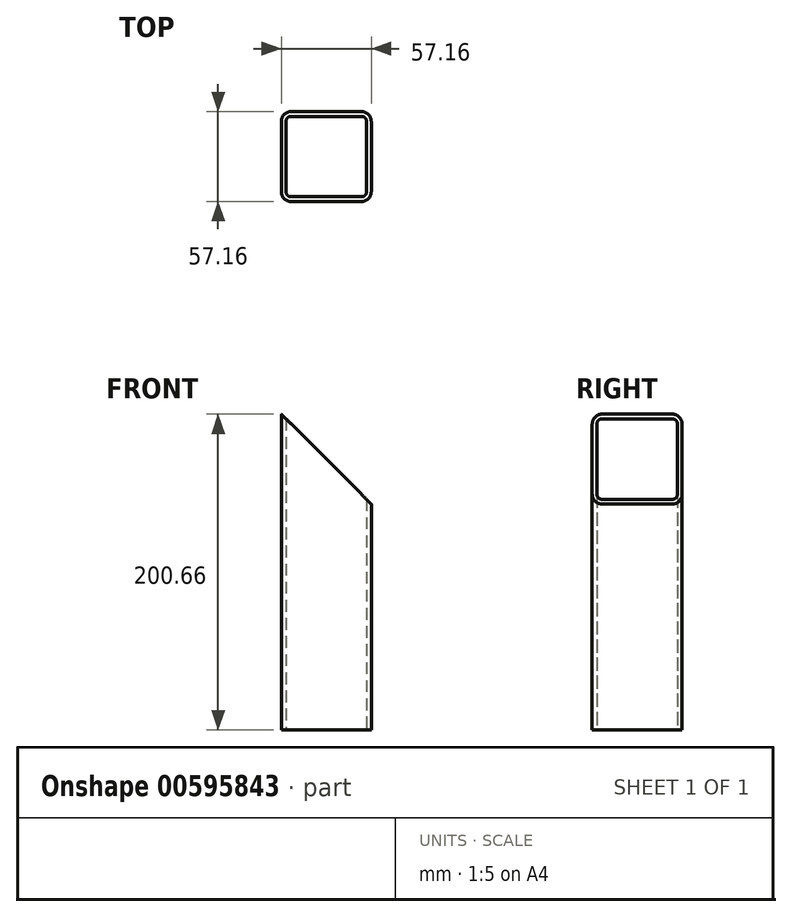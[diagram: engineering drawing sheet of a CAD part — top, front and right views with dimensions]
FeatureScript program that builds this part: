
annotation { "Feature Type Name" : "Feature", "Feature Type Description" : "" }
export const myFeature = defineFeature(function(context is Context, id is Id, definition is map)
    precondition{}
    {
        {
            var Q0;
            Q0=qCreatedBy(makeId("Top.planeOp"),FACE);
            var sketch = newSketch(context, id + "F0", { "sketchPlane" : qUnion([Q0])});
            skLineSegment(sketch, "E0.bottom", {"start": v(28.58, -28.58) * mm, "end": v(-28.58, -28.58) * mm});
            skLineSegment(sketch, "E0.top", {"start": v(28.58, 28.58) * mm, "end": v(-28.58, 28.58) * mm});
            skLineSegment(sketch, "E0.left", {"start": v(28.58, -28.58) * mm, "end": v(28.58, 28.58) * mm});
            skLineSegment(sketch, "E0.right", {"start": v(-28.57, -28.58) * mm, "end": v(-28.58, 28.58) * mm});
            skPoint(sketch, "E0.middle", {"position": v(0, 0) * mm});
            skLineSegment(sketch, "E1.bottom", {"start": v(-25.53, 25.53) * mm, "end": v(25.53, 25.53) * mm});
            skLineSegment(sketch, "E1.top", {"start": v(-25.53, -25.53) * mm, "end": v(25.53, -25.53) * mm});
            skLineSegment(sketch, "E1.left", {"start": v(-25.53, 25.53) * mm, "end": v(-25.53, -25.53) * mm});
            skLineSegment(sketch, "E1.right", {"start": v(25.53, 25.53) * mm, "end": v(25.53, -25.53) * mm});
            skSolve(sketch);
        }
        {
            var Q0;
            Q0=qSketchRegion(id+"F0",true);
            extrude(context, id + "F1", {"entities" : qUnion([Q0]), "depth" : 200.66 * mm, "offsetDistance" : 25.4 * mm});
        }
        {
            var Q0;
            Q0=makeQuery(id+"F1.opExtrude","SWEPT_EDGE",EDGE,{"disambiguationData":[OSD([sQuery(id+"F0.wireOp",EDGE,"E1.bottom"),sQuery(id+"F0.wireOp",EDGE,"E1.right")])]});
            var Q1;
            Q1=makeQuery(id+"F1.opExtrude","SWEPT_EDGE",EDGE,{"disambiguationData":[OSD([sQuery(id+"F0.wireOp",EDGE,"E1.bottom"),sQuery(id+"F0.wireOp",EDGE,"E1.left")])]});
            var Q2;
            Q2=makeQuery(id+"F1.opExtrude","SWEPT_EDGE",EDGE,{"disambiguationData":[OSD([sQuery(id+"F0.wireOp",EDGE,"E1.top"),sQuery(id+"F0.wireOp",EDGE,"E1.left")])]});
            var Q3;
            Q3=makeQuery(id+"F1.opExtrude","SWEPT_EDGE",EDGE,{"disambiguationData":[OSD([sQuery(id+"F0.wireOp",EDGE,"E1.top"),sQuery(id+"F0.wireOp",EDGE,"E1.right")])]});
            fillet(context, id + "F2", {"entities" : qUnion([Q0, Q1, Q2, Q3]), "radius" : 3.05 * mm, "tangentPropagation" : true, "allowEdgeOverflow" : false});
        }
        {
            var Q0;
            Q0=makeQuery(id+"F1.opExtrude","SWEPT_EDGE",EDGE,{"disambiguationData":[OSD([sQuery(id+"F0.wireOp",EDGE,"E0.top"),sQuery(id+"F0.wireOp",EDGE,"E0.right")])]});
            var Q1;
            Q1=makeQuery(id+"F1.opExtrude","SWEPT_EDGE",EDGE,{"disambiguationData":[OSD([sQuery(id+"F0.wireOp",EDGE,"E0.bottom"),sQuery(id+"F0.wireOp",EDGE,"E0.right")])]});
            var Q2;
            Q2=makeQuery(id+"F1.opExtrude","SWEPT_EDGE",EDGE,{"disambiguationData":[OSD([sQuery(id+"F0.wireOp",EDGE,"E0.bottom"),sQuery(id+"F0.wireOp",EDGE,"E0.left")])]});
            var Q3;
            Q3=makeQuery(id+"F1.opExtrude","SWEPT_EDGE",EDGE,{"disambiguationData":[OSD([sQuery(id+"F0.wireOp",EDGE,"E0.top"),sQuery(id+"F0.wireOp",EDGE,"E0.left")])]});
            fillet(context, id + "F3", {"entities" : qUnion([Q0, Q1, Q2, Q3]), "radius" : 6.35 * mm, "tangentPropagation" : true, "allowEdgeOverflow" : false});
        }
        {
            var Q0;
            Q0=qCreatedBy(makeId("Front.planeOp"),FACE);
            var sketch = newSketch(context, id + "F4", { "sketchPlane" : qUnion([Q0])});
            skLineSegment(sketch, "E2", {"start": v(28.58, 143.51) * mm, "end": v(-28.58, 200.66) * mm});
            skLineSegment(sketch, "E3", {"start": v(-28.58, 200.66) * mm, "end": v(28.58, 200.66) * mm});
            skLineSegment(sketch, "E4", {"start": v(28.58, 200.66) * mm, "end": v(28.58, 143.51) * mm});
            skSolve(sketch);
        }
        {
            var Q0;
            Q0=qSketchRegion(id+"F4",true);
            extrude(context, id + "F5", {"entities" : qUnion([Q0]), "operationType" : NewBodyOperationType.REMOVE, "endBound" : BoundingType.THROUGH_ALL, "oppositeDirection" : true, "depth" : 25.4 * mm, "offsetDistance" : 25.4 * mm, "hasSecondDirection" : true, "secondDirectionBound" : SecondDirectionBoundingType.THROUGH_ALL, "secondDirectionOppositeDirection" : false, "secondDirectionDepth" : 25.4 * mm});
        }
    });
